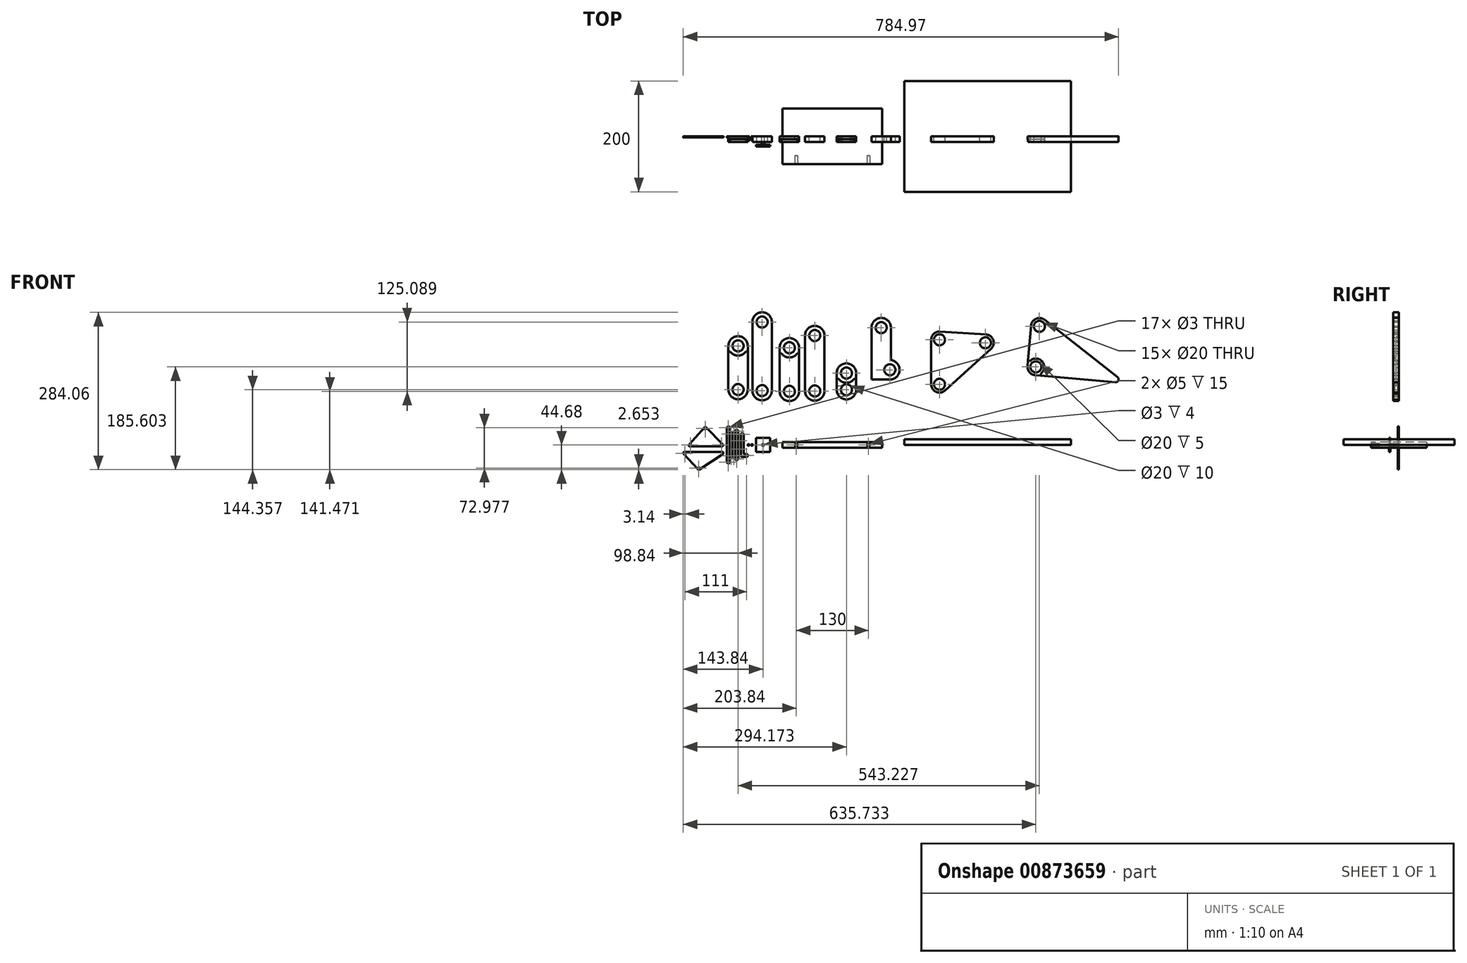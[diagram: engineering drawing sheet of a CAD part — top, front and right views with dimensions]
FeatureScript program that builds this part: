
annotation { "Feature Type Name" : "Feature", "Feature Type Description" : "" }
export const myFeature = defineFeature(function(context is Context, id is Id, definition is map)
    precondition{}
    {
        {
            var Q0;
            Q0=qCreatedBy(makeId("Front.planeOp"),FACE);
            var sketch = newSketch(context, id + "F0", { "sketchPlane" : qUnion([Q0])});
            skLineSegment(sketch, "E0", {"start": v(0, 7.5) * mm, "end": v(0, -7.5) * mm});
            skLineSegment(sketch, "E1", {"start": v(5, 7.5) * mm, "end": v(5, -7.5) * mm});
            skArc(sketch, "E2", {"start": v(5, 7.5) * mm, "mid": v(2.5, 10) * mm, "end": v(0, 7.5) * mm});
            skArc(sketch, "E3", {"start": v(0, -7.5) * mm, "mid": v(2.5, -10) * mm, "end": v(5, -7.5) * mm});
            skCircle(sketch, "E4", {"center": v(2.5, 7.5) * mm, "radius": 1.5 * mm});
            skCircle(sketch, "E5", {"center": v(2.5, -7.5) * mm, "radius": 1.5 * mm});
            skSolve(sketch);
        }
        {
            var Q0;
            Q0=makeQuery(id+"F0.imprint","IMPRINT",FACE,{"disambiguationData":[TD([[makeQuery(id+"F0.imprint","IMPRINT",EDGE,{"derivedFrom":sQuery(id+"F0.wireOp",EDGE,"E0")}),1.0]])]});
            extrude(context, id + "F1", {"entities" : qUnion([Q0]), "depth" : 2 * mm});
        }
        {
            var Q0;
            Q0=qCreatedBy(makeId("Front.planeOp"),FACE);
            var sketch = newSketch(context, id + "F2", { "sketchPlane" : qUnion([Q0])});
            skLineSegment(sketch, "E6", {"start": v(0, 25) * mm, "end": v(0, -25) * mm});
            skLineSegment(sketch, "E7", {"start": v(-5, 25) * mm, "end": v(-5, -25) * mm});
            skArc(sketch, "E8", {"start": v(0, 25) * mm, "mid": v(-2.5, 27.5) * mm, "end": v(-5, 25) * mm});
            skArc(sketch, "E9", {"start": v(-5, -25) * mm, "mid": v(-2.5, -27.5) * mm, "end": v(0, -25) * mm});
            skCircle(sketch, "E10", {"center": v(-2.5, 25) * mm, "radius": 1.5 * mm});
            skCircle(sketch, "E11", {"center": v(-2.5, -25) * mm, "radius": 1.5 * mm});
            skSolve(sketch);
        }
        {
            var Q0;
            Q0=makeQuery(id+"F2.imprint","IMPRINT",FACE,{"disambiguationData":[TD([[makeQuery(id+"F2.imprint","IMPRINT",EDGE,{"derivedFrom":sQuery(id+"F2.wireOp",EDGE,"E6")}),-1.0]])]});
            extrude(context, id + "F3", {"entities" : qUnion([Q0]), "depth" : 2 * mm});
        }
        {
            var Q0;
            Q0=qCreatedBy(makeId("Front.planeOp"),FACE);
            var sketch = newSketch(context, id + "F4", { "sketchPlane" : qUnion([Q0])});
            skLineSegment(sketch, "E12", {"start": v(-5, 19.65) * mm, "end": v(-5, -19.65) * mm});
            skLineSegment(sketch, "E13", {"start": v(-10, 19.65) * mm, "end": v(-10, -19.65) * mm});
            skArc(sketch, "E14", {"start": v(-5, 19.65) * mm, "mid": v(-7.5, 22.15) * mm, "end": v(-10, 19.65) * mm});
            skArc(sketch, "E15", {"start": v(-10, -19.65) * mm, "mid": v(-7.5, -22.15) * mm, "end": v(-5, -19.65) * mm});
            skCircle(sketch, "E16", {"center": v(-7.5, 19.65) * mm, "radius": 1.5 * mm});
            skCircle(sketch, "E17", {"center": v(-7.5, -19.65) * mm, "radius": 1.5 * mm});
            skSolve(sketch);
        }
        {
            var Q0;
            Q0=makeQuery(id+"F4.imprint","IMPRINT",FACE,{"disambiguationData":[TD([[makeQuery(id+"F4.imprint","IMPRINT",EDGE,{"derivedFrom":sQuery(id+"F4.wireOp",EDGE,"E12")}),-1.0]])]});
            extrude(context, id + "F5", {"entities" : qUnion([Q0]), "depth" : 2 * mm});
        }
        {
            var Q0;
            Q0=qCreatedBy(makeId("Front.planeOp"),FACE);
            var sketch = newSketch(context, id + "F6", { "sketchPlane" : qUnion([Q0])});
            skLineSegment(sketch, "E18", {"start": v(-10, 19.7) * mm, "end": v(-10, -19.7) * mm});
            skLineSegment(sketch, "E19", {"start": v(-15, 19.7) * mm, "end": v(-15, -19.7) * mm});
            skArc(sketch, "E20", {"start": v(-10, 19.7) * mm, "mid": v(-12.5, 22.2) * mm, "end": v(-15, 19.7) * mm});
            skArc(sketch, "E21", {"start": v(-15, -19.7) * mm, "mid": v(-12.5, -22.2) * mm, "end": v(-10, -19.7) * mm});
            skCircle(sketch, "E22", {"center": v(-12.5, 19.7) * mm, "radius": 1.5 * mm});
            skCircle(sketch, "E23", {"center": v(-12.5, -19.7) * mm, "radius": 1.5 * mm});
            skSolve(sketch);
        }
        {
            var Q0;
            Q0=makeQuery(id+"F6.imprint","IMPRINT",FACE,{"disambiguationData":[TD([[makeQuery(id+"F6.imprint","IMPRINT",EDGE,{"derivedFrom":sQuery(id+"F6.wireOp",EDGE,"E18")}),-1.0]])]});
            extrude(context, id + "F7", {"entities" : qUnion([Q0]), "depth" : 2 * mm});
        }
        {
            var Q0;
            Q0=qCreatedBy(makeId("Front.planeOp"),FACE);
            var sketch = newSketch(context, id + "F8", { "sketchPlane" : qUnion([Q0])});
            skLineSegment(sketch, "E24", {"start": v(-20, 30.95) * mm, "end": v(-20, -30.95) * mm});
            skLineSegment(sketch, "E25", {"start": v(-15, 30.95) * mm, "end": v(-15, -30.95) * mm});
            skArc(sketch, "E26", {"start": v(-15, 30.95) * mm, "mid": v(-17.5, 33.45) * mm, "end": v(-20, 30.95) * mm});
            skArc(sketch, "E27", {"start": v(-20, -30.95) * mm, "mid": v(-17.5, -33.45) * mm, "end": v(-15, -30.95) * mm});
            skCircle(sketch, "E28", {"center": v(-17.5, -30.95) * mm, "radius": 1.5 * mm});
            skCircle(sketch, "E29", {"center": v(-17.5, 30.95) * mm, "radius": 1.5 * mm});
            skSolve(sketch);
        }
        {
            var Q0;
            Q0=makeQuery(id+"F8.imprint","IMPRINT",FACE,{"disambiguationData":[TD([[makeQuery(id+"F8.imprint","IMPRINT",EDGE,{"derivedFrom":sQuery(id+"F8.wireOp",EDGE,"E24")}),1.0]])]});
            extrude(context, id + "F9", {"entities" : qUnion([Q0]), "depth" : 2 * mm});
        }
        {
            var Q0;
            Q0=qCreatedBy(makeId("Front.planeOp"),FACE);
            var sketch = newSketch(context, id + "F10", { "sketchPlane" : qUnion([Q0])});
            skLineSegment(sketch, "E30", {"start": v(-58.92, 29.76) * mm, "end": v(-30, 0) * mm, "construction": true});
            skLineSegment(sketch, "E31", {"start": v(-30, 0) * mm, "end": v(-85.8, 0) * mm, "construction": true});
            skLineSegment(sketch, "E32", {"start": v(-85.8, 0) * mm, "end": v(-58.92, 29.76) * mm, "construction": true});
            skCircle(sketch, "E33", {"center": v(-85.8, 0) * mm, "radius": 1.5 * mm});
            skCircle(sketch, "E34", {"center": v(-30, 0) * mm, "radius": 1.5 * mm});
            skCircle(sketch, "E35", {"center": v(-58.92, 29.76) * mm, "radius": 1.5 * mm});
            skLineSegment(sketch, "E36", {"start": v(-91.43, -2.5) * mm, "end": v(-24.08, -2.5) * mm});
            skLineSegment(sketch, "E37", {"start": v(-59, 33.42) * mm, "end": v(-91.43, -2.5) * mm});
            skLineSegment(sketch, "E38", {"start": v(-59, 33.42) * mm, "end": v(-24.08, -2.5) * mm});
            skSolve(sketch);
        }
        {
            var Q0;
            Q0=makeQuery(id+"F10.imprint","IMPRINT",FACE,{"disambiguationData":[TD([[makeQuery(id+"F10.imprint","IMPRINT",EDGE,{"derivedFrom":sQuery(id+"F10.wireOp",EDGE,"E33")}),-1.0]])]});
            extrude(context, id + "F11", {"entities" : qUnion([Q0]), "depth" : 2 * mm});
        }
        {
            var Q0;
            Q0=makeQuery(id+"F11.opExtrude","SWEPT_EDGE",EDGE,{"disambiguationData":[OSD([sQuery(id+"F10.wireOp",EDGE,"E36"),sQuery(id+"F10.wireOp",EDGE,"E37")])]});
            var Q1;
            Q1=makeQuery(id+"F11.opExtrude","SWEPT_EDGE",EDGE,{"disambiguationData":[OSD([sQuery(id+"F10.wireOp",EDGE,"E36"),sQuery(id+"F10.wireOp",EDGE,"E38")])]});
            var Q2;
            Q2=makeQuery(id+"F11.opExtrude","SWEPT_EDGE",EDGE,{"disambiguationData":[OSD([sQuery(id+"F10.wireOp",EDGE,"E37"),sQuery(id+"F10.wireOp",EDGE,"E38")])]});
            fillet(context, id + "F12", {"entities" : qUnion([Q0, Q1, Q2]), "radius" : 2 * mm, "tangentPropagation" : true, "allowEdgeOverflow" : false});
        }
        {
            var Q0;
            Q0=qCreatedBy(makeId("Front.planeOp"),FACE);
            var sketch = newSketch(context, id + "F13", { "sketchPlane" : qUnion([Q0])});
            skLineSegment(sketch, "E39", {"start": v(-95.7, -15) * mm, "end": v(-30, -15) * mm, "construction": true});
            skLineSegment(sketch, "E40", {"start": v(-30, -15) * mm, "end": v(-70.87, -42.03) * mm, "construction": true});
            skLineSegment(sketch, "E41", {"start": v(-70.87, -42.03) * mm, "end": v(-95.7, -15) * mm, "construction": true});
            skCircle(sketch, "E42", {"center": v(-95.7, -15) * mm, "radius": 1.5 * mm});
            skCircle(sketch, "E43", {"center": v(-70.87, -42.03) * mm, "radius": 1.5 * mm});
            skLineSegment(sketch, "E44", {"start": v(-101.4, -12.5) * mm, "end": v(-21.69, -12.5) * mm});
            skLineSegment(sketch, "E45", {"start": v(-21.69, -12.5) * mm, "end": v(-71.27, -45.29) * mm});
            skLineSegment(sketch, "E46", {"start": v(-71.27, -45.29) * mm, "end": v(-101.4, -12.5) * mm});
            skSolve(sketch);
        }
        {
            var Q0;
            Q0=makeQuery(id+"F13.imprint","IMPRINT",FACE,{"disambiguationData":[TD([[makeQuery(id+"F13.imprint","IMPRINT",EDGE,{"derivedFrom":sQuery(id+"F13.wireOp",EDGE,"E42")}),-1.0]])]});
            extrude(context, id + "F14", {"entities" : qUnion([Q0]), "depth" : 2 * mm});
        }
        {
            var Q0;
            Q0=makeQuery(id+"F14.opExtrude","SWEPT_EDGE",EDGE,{"disambiguationData":[OSD([sQuery(id+"F13.wireOp",EDGE,"E44"),sQuery(id+"F13.wireOp",EDGE,"E46")])]});
            var Q1;
            Q1=makeQuery(id+"F14.opExtrude","SWEPT_EDGE",EDGE,{"disambiguationData":[OSD([sQuery(id+"F13.wireOp",EDGE,"E45"),sQuery(id+"F13.wireOp",EDGE,"E46")])]});
            var Q2;
            Q2=makeQuery(id+"F14.opExtrude","SWEPT_EDGE",EDGE,{"disambiguationData":[OSD([sQuery(id+"F13.wireOp",EDGE,"E44"),sQuery(id+"F13.wireOp",EDGE,"E45")])]});
            fillet(context, id + "F15", {"entities" : qUnion([Q0, Q1, Q2]), "radius" : 2 * mm, "tangentPropagation" : true, "allowEdgeOverflow" : false});
        }
        {
            var Q0;
            Q0=qCreatedBy(makeId("Front.planeOp"),FACE);
            var sketch = newSketch(context, id + "F16", { "sketchPlane" : qUnion([Q0])});
            skLineSegment(sketch, "E47", {"start": v(7.5, 19) * mm, "end": v(7.5, -19) * mm, "construction": true});
            skLineSegment(sketch, "E48", {"start": v(7.5, -19) * mm, "end": v(15.3, -19) * mm, "construction": true});
            skArc(sketch, "E49", {"start": v(10, 19) * mm, "mid": v(7.5, 21.5) * mm, "end": v(5, 19) * mm});
            skArc(sketch, "E50", {"start": v(15.3, -21.5) * mm, "mid": v(17.8, -19) * mm, "end": v(15.3, -16.5) * mm});
            skLineSegment(sketch, "E51", {"start": v(5, 19) * mm, "end": v(5, -21.5) * mm});
            skLineSegment(sketch, "E52", {"start": v(15.3, -21.5) * mm, "end": v(5, -21.5) * mm});
            skLineSegment(sketch, "E53", {"start": v(10, 19) * mm, "end": v(10, -16.5) * mm});
            skLineSegment(sketch, "E54", {"start": v(15.3, -16.5) * mm, "end": v(10, -16.5) * mm});
            skCircle(sketch, "E55", {"center": v(7.5, 19) * mm, "radius": 1.5 * mm});
            skCircle(sketch, "E56", {"center": v(15.3, -19) * mm, "radius": 1.5 * mm});
            skSolve(sketch);
        }
        {
            var Q0;
            Q0=makeQuery(id+"F16.imprint","IMPRINT",FACE,{"disambiguationData":[TD([[makeQuery(id+"F16.imprint","IMPRINT",EDGE,{"derivedFrom":sQuery(id+"F16.wireOp",EDGE,"E49")}),1.0]])]});
            extrude(context, id + "F17", {"entities" : qUnion([Q0]), "depth" : 2 * mm});
        }
        {
            var Q0;
            Q0=qCreatedBy(makeId("Front.planeOp"),FACE);
            var sketch = newSketch(context, id + "F18", { "sketchPlane" : qUnion([Q0])});
            skCircle(sketch, "E57", {"center": v(24.95, 0) * mm, "radius": 1.5 * mm});
            skSolve(sketch);
        }
        {
            var Q0;
            Q0=makeQuery(id+"F18.imprint","IMPRINT",FACE,{"disambiguationData":[TD([[makeQuery(id+"F18.imprint","IMPRINT",EDGE,{"derivedFrom":sQuery(id+"F18.wireOp",EDGE,"E57")}),1.0]])]});
            extrude(context, id + "F19", {"entities" : qUnion([Q0]), "depth" : 6 * mm});
        }
        {
            var Q0;
            Q0=qCreatedBy(makeId("Front.planeOp"),FACE);
            var sketch = newSketch(context, id + "F20", { "sketchPlane" : qUnion([Q0])});
            skCircle(sketch, "E58", {"center": v(45, 0) * mm, "radius": 2.5 * mm});
            skSolve(sketch);
        }
        {
            var Q0;
            Q0=makeQuery(id+"F20.imprint","IMPRINT",FACE,{"disambiguationData":[TD([[makeQuery(id+"F20.imprint","IMPRINT",EDGE,{"derivedFrom":sQuery(id+"F20.wireOp",EDGE,"E58")}),1.0]])]});
            extrude(context, id + "F21", {"entities" : qUnion([Q0]), "depth" : 15 * mm, "offsetDistance" : 25 * mm});
        }
        {
            var Q0;
            Q0=makeQuery(id+"F21.opExtrude","CAP_FACE",FACE,{"disambiguationData":[OSD([sQuery(id+"F20.wireOp",EDGE,"E58")])],"isStart":false});
            var sketch = newSketch(context, id + "F22", { "sketchPlane" : qUnion([Q0])});
            skLineSegment(sketch, "E59.bottom", {"start": v(32.5, 12.5) * mm, "end": v(57.5, 12.5) * mm});
            skLineSegment(sketch, "E59.top", {"start": v(32.5, -12.5) * mm, "end": v(57.5, -12.5) * mm});
            skLineSegment(sketch, "E59.left", {"start": v(32.5, 12.5) * mm, "end": v(32.5, -12.5) * mm});
            skLineSegment(sketch, "E59.right", {"start": v(57.5, 12.5) * mm, "end": v(57.5, -12.5) * mm});
            skCircle(sketch, "E60.0", {"center": v(45, 0) * mm, "radius": 2.5 * mm, "construction": true});
            skSolve(sketch);
        }
        {
            var Q0;
            Q0=makeQuery(id+"F22.imprint","IMPRINT",FACE,{"disambiguationData":[TD([[makeQuery(id+"F22.imprint","IMPRINT",EDGE,{"derivedFrom":sQuery(id+"F22.wireOp",EDGE,"E59.bottom")}),-1.0]])]});
            var Q1;
            Q1=makeQuery(id+"F22.imprint","IMPRINT",FACE,{"disambiguationData":[TD([[makeQuery(id+"F22.imprint","IMPRINT",EDGE,{"derivedFrom":makeQuery(id+"F21.opExtrude","CAP_EDGE",EDGE,{"disambiguationData":[OSD([sQuery(id+"F20.wireOp",EDGE,"E58")])],"isStart":false})}),1.0]])]});
            extrude(context, id + "F23", {"entities" : qUnion([Q0, Q1]), "operationType" : NewBodyOperationType.ADD, "depth" : 3 * mm});
        }
        {
            var Q0;
            Q0=makeQuery(id+"F23.opExtrude","CAP_FACE",FACE,{"disambiguationData":[OSD([sQuery(id+"F22.wireOp",EDGE,"E59.bottom"),sQuery(id+"F22.wireOp",EDGE,"E59.top"),sQuery(id+"F22.wireOp",EDGE,"E59.left"),sQuery(id+"F22.wireOp",EDGE,"E59.right")])],"isStart":false});
            var sketch = newSketch(context, id + "F24", { "sketchPlane" : qUnion([Q0])});
            skCircle(sketch, "E61", {"center": v(45, 0) * mm, "radius": 1.5 * mm});
            skSolve(sketch);
        }
        {
            var Q0;
            Q0=makeQuery(id+"F24.imprint","IMPRINT",FACE,{"disambiguationData":[TD([[makeQuery(id+"F24.imprint","IMPRINT",EDGE,{"derivedFrom":sQuery(id+"F24.wireOp",EDGE,"E61")}),1.0]])]});
            extrude(context, id + "F25", {"entities" : qUnion([Q0]), "operationType" : NewBodyOperationType.REMOVE, "oppositeDirection" : true, "depth" : 4 * mm});
        }
        {
            var Q0;
            Q0=qCreatedBy(makeId("Front.planeOp"),FACE);
            var sketch = newSketch(context, id + "F26", { "sketchPlane" : qUnion([Q0])});
            skCircle(sketch, "E62", {"center": v(18.95, 0) * mm, "radius": 1.5 * mm});
            skSolve(sketch);
        }
        {
            var Q0;
            Q0=makeQuery(id+"F26.imprint","IMPRINT",FACE,{"disambiguationData":[TD([[makeQuery(id+"F26.imprint","IMPRINT",EDGE,{"derivedFrom":sQuery(id+"F26.wireOp",EDGE,"E62")}),1.0]])]});
            extrude(context, id + "F27", {"entities" : qUnion([Q0]), "depth" : 8 * mm});
        }
        {
            var Q0;
            Q0=qCreatedBy(makeId("Top.planeOp"),FACE);
            var sketch = newSketch(context, id + "F28", { "sketchPlane" : qUnion([Q0])});
            skLineSegment(sketch, "E63.bottom", {"start": v(80, 50) * mm, "end": v(260, 50) * mm});
            skLineSegment(sketch, "E63.top", {"start": v(80, -50) * mm, "end": v(260, -50) * mm});
            skLineSegment(sketch, "E63.left", {"start": v(80, 50) * mm, "end": v(80, -50) * mm});
            skLineSegment(sketch, "E63.right", {"start": v(260, 50) * mm, "end": v(260, -50) * mm});
            skSolve(sketch);
        }
        {
            var Q0;
            Q0=qSketchRegion(id+"F28",true);
            extrude(context, id + "F29", {"entities" : qUnion([Q0]), "depth" : 5 * mm, "offsetDistance" : 25 * mm, "hasSecondDirection" : true, "secondDirectionOppositeDirection" : true, "secondDirectionDepth" : 5 * mm});
        }
        {
            var Q0;
            Q0=makeQuery(id+"F29.opExtrude","SWEPT_FACE",FACE,{"disambiguationData":[OSD([sQuery(id+"F28.wireOp",EDGE,"E63.top")])]});
            var sketch = newSketch(context, id + "F30", { "sketchPlane" : qUnion([Q0])});
            skCircle(sketch, "E64", {"center": v(105, 0) * mm, "radius": 2.5 * mm});
            skPoint(sketch, "E64.centerSnap0", {"position": v(80, 0) * mm});
            skCircle(sketch, "E65", {"center": v(235, 0) * mm, "radius": 2.5 * mm});
            skSolve(sketch);
        }
        {
            var Q0;
            Q0=qSketchRegion(id+"F30",true);
            extrude(context, id + "F31", {"entities" : qUnion([Q0]), "operationType" : NewBodyOperationType.REMOVE, "oppositeDirection" : true, "depth" : 15 * mm, "offsetDistance" : 25 * mm});
        }
        {
            var Q0;
            Q0=qCreatedBy(makeId("Top.planeOp"),FACE);
            var sketch = newSketch(context, id + "F32", { "sketchPlane" : qUnion([Q0])});
            skLineSegment(sketch, "E66.bottom", {"start": v(300, 100) * mm, "end": v(600, 100) * mm});
            skLineSegment(sketch, "E66.top", {"start": v(300, -100) * mm, "end": v(600, -100) * mm});
            skLineSegment(sketch, "E66.left", {"start": v(300, 100) * mm, "end": v(300, -100) * mm});
            skLineSegment(sketch, "E66.right", {"start": v(600, 100) * mm, "end": v(600, -100) * mm});
            skSolve(sketch);
        }
        {
            var Q0;
            Q0=qSketchRegion(id+"F32",true);
            extrude(context, id + "F33", {"entities" : qUnion([Q0]), "depth" : 10 * mm, "offsetDistance" : 25 * mm});
        }
        {
            var Q0;
            Q0=qCreatedBy(makeId("Front.planeOp"),FACE);
            var sketch = newSketch(context, id + "F34", { "sketchPlane" : qUnion([Q0])});
            skCircle(sketch, "E67", {"center": v(0, 178.8) * mm, "radius": 10 * mm});
            skCircle(sketch, "E68", {"center": v(0, 100) * mm, "radius": 10 * mm});
            skArc(sketch, "E69", {"start": v(17.5, 178.8) * mm, "mid": v(0, 196.3) * mm, "end": v(-17.5, 178.8) * mm});
            skArc(sketch, "E70", {"start": v(-17.5, 100) * mm, "mid": v(0, 82.5) * mm, "end": v(17.5, 100) * mm});
            skLineSegment(sketch, "E71", {"start": v(-17.5, 178.8) * mm, "end": v(-17.5, 100) * mm});
            skLineSegment(sketch, "E72", {"start": v(17.5, 178.8) * mm, "end": v(17.5, 100) * mm});
            skSolve(sketch);
        }
        {
            var Q0;
            Q0=qSketchRegion(id+"F34",true);
            extrude(context, id + "F35", {"entities" : qUnion([Q0]), "depth" : 10 * mm, "offsetDistance" : 25 * mm});
        }
        {
            var Q0;
            Q0=qCreatedBy(makeId("Front.planeOp"),FACE);
            var sketch = newSketch(context, id + "F36", { "sketchPlane" : qUnion([Q0])});
            skCircle(sketch, "E73", {"center": v(43.37, 98.08) * mm, "radius": 10 * mm});
            skArc(sketch, "E74", {"start": v(25.87, 98.08) * mm, "mid": v(43.37, 80.58) * mm, "end": v(60.87, 98.08) * mm});
            skArc(sketch, "E75", {"start": v(60.87, 221.88) * mm, "mid": v(43.37, 239.38) * mm, "end": v(25.87, 221.88) * mm});
            skCircle(sketch, "E76", {"center": v(43.37, 221.88) * mm, "radius": 10 * mm});
            skLineSegment(sketch, "E77", {"start": v(25.87, 221.88) * mm, "end": v(25.87, 98.08) * mm});
            skLineSegment(sketch, "E78", {"start": v(60.87, 221.88) * mm, "end": v(60.87, 98.08) * mm});
            skSolve(sketch);
        }
        {
            var Q0;
            Q0=qSketchRegion(id+"F36",true);
            extrude(context, id + "F37", {"entities" : qUnion([Q0]), "depth" : 10 * mm, "offsetDistance" : 25 * mm});
        }
        {
            var Q0;
            Q0=qCreatedBy(makeId("Front.planeOp"),FACE);
            var sketch = newSketch(context, id + "F38", { "sketchPlane" : qUnion([Q0])});
            skCircle(sketch, "E79", {"center": v(92.5, 96.8) * mm, "radius": 10 * mm});
            skCircle(sketch, "E80", {"center": v(92.5, 175.4) * mm, "radius": 10 * mm});
            skArc(sketch, "E81", {"start": v(110, 175.4) * mm, "mid": v(92.5, 192.9) * mm, "end": v(75, 175.4) * mm});
            skArc(sketch, "E82", {"start": v(75, 96.8) * mm, "mid": v(92.5, 79.3) * mm, "end": v(110, 96.8) * mm});
            skLineSegment(sketch, "E83", {"start": v(75, 175.4) * mm, "end": v(75, 96.8) * mm});
            skLineSegment(sketch, "E84", {"start": v(110, 175.4) * mm, "end": v(110, 96.8) * mm});
            skSolve(sketch);
        }
        {
            var Q0;
            Q0=qSketchRegion(id+"F38",true);
            extrude(context, id + "F39", {"entities" : qUnion([Q0]), "depth" : 10 * mm, "offsetDistance" : 25 * mm});
        }
        {
            var Q0;
            Q0=qCreatedBy(makeId("Front.planeOp"),FACE);
            var sketch = newSketch(context, id + "F40", { "sketchPlane" : qUnion([Q0])});
            skCircle(sketch, "E85", {"center": v(138.24, 97.46) * mm, "radius": 10 * mm});
            skCircle(sketch, "E86", {"center": v(138.24, 197.46) * mm, "radius": 10 * mm});
            skArc(sketch, "E87", {"start": v(155.74, 197.46) * mm, "mid": v(138.24, 214.96) * mm, "end": v(120.74, 197.46) * mm});
            skArc(sketch, "E88", {"start": v(120.74, 97.46) * mm, "mid": v(138.24, 79.96) * mm, "end": v(155.74, 97.46) * mm});
            skLineSegment(sketch, "E89", {"start": v(120.74, 197.46) * mm, "end": v(120.74, 97.46) * mm});
            skLineSegment(sketch, "E90", {"start": v(155.74, 197.46) * mm, "end": v(155.74, 97.46) * mm});
            skSolve(sketch);
        }
        {
            var Q0;
            Q0=qSketchRegion(id+"F40",true);
            extrude(context, id + "F41", {"entities" : qUnion([Q0]), "depth" : 10 * mm, "offsetDistance" : 25 * mm});
        }
        {
            var Q0;
            Q0=qCreatedBy(makeId("Front.planeOp"),FACE);
            var sketch = newSketch(context, id + "F42", { "sketchPlane" : qUnion([Q0])});
            skCircle(sketch, "E91", {"center": v(195.33, 99.68) * mm, "radius": 10 * mm});
            skCircle(sketch, "E92", {"center": v(195.33, 129.68) * mm, "radius": 10 * mm});
            skArc(sketch, "E93", {"start": v(212.83, 129.68) * mm, "mid": v(195.33, 147.18) * mm, "end": v(177.83, 129.68) * mm});
            skArc(sketch, "E94", {"start": v(177.83, 99.68) * mm, "mid": v(195.33, 82.18) * mm, "end": v(212.83, 99.68) * mm});
            skLineSegment(sketch, "E95", {"start": v(177.83, 129.68) * mm, "end": v(177.83, 99.68) * mm});
            skLineSegment(sketch, "E96", {"start": v(212.83, 129.68) * mm, "end": v(212.83, 99.68) * mm});
            skSolve(sketch);
        }
        {
            var Q0;
            Q0=qSketchRegion(id+"F42",true);
            extrude(context, id + "F43", {"entities" : qUnion([Q0]), "depth" : 10 * mm, "offsetDistance" : 25 * mm});
        }
        {
            var Q0;
            Q0=qCreatedBy(makeId("Front.planeOp"),FACE);
            var sketch = newSketch(context, id + "F44", { "sketchPlane" : qUnion([Q0])});
            skLineSegment(sketch, "E97", {"start": v(258.08, 211.66) * mm, "end": v(258.08, 135.66) * mm, "construction": true});
            skLineSegment(sketch, "E98", {"start": v(258.08, 135.66) * mm, "end": v(273.68, 135.66) * mm, "construction": true});
            skCircle(sketch, "E99", {"center": v(258.08, 211.66) * mm, "radius": 10 * mm});
            skCircle(sketch, "E100", {"center": v(273.68, 135.66) * mm, "radius": 10 * mm});
            skArc(sketch, "E101", {"start": v(275.58, 211.66) * mm, "mid": v(258.08, 229.16) * mm, "end": v(240.58, 211.66) * mm});
            skArc(sketch, "E102", {"start": v(273.68, 118.16) * mm, "mid": v(291.15, 134.7) * mm, "end": v(275.58, 153.05) * mm});
            skLineSegment(sketch, "E103", {"start": v(275.58, 211.66) * mm, "end": v(275.58, 153.05) * mm});
            skLineSegment(sketch, "E104", {"start": v(240.58, 211.66) * mm, "end": v(240.58, 118.16) * mm});
            skLineSegment(sketch, "E105", {"start": v(240.58, 118.16) * mm, "end": v(273.68, 118.16) * mm});
            skSolve(sketch);
        }
        {
            var Q0;
            Q0=qSketchRegion(id+"F44",true);
            extrude(context, id + "F45", {"entities" : qUnion([Q0]), "depth" : 10 * mm, "offsetDistance" : 25 * mm});
        }
        {
            var Q0;
            Q0=qCreatedBy(makeId("Front.planeOp"),FACE);
            var sketch = newSketch(context, id + "F46", { "sketchPlane" : qUnion([Q0])});
            skLineSegment(sketch, "E106", {"start": v(363.12, 189.73) * mm, "end": v(363.12, 109.53) * mm, "construction": true});
            skLineSegment(sketch, "E107", {"start": v(363.12, 109.53) * mm, "end": v(445.94, 184.33) * mm, "construction": true});
            skLineSegment(sketch, "E108", {"start": v(445.94, 184.33) * mm, "end": v(363.12, 189.73) * mm, "construction": true});
            skCircle(sketch, "E109", {"center": v(363.12, 189.73) * mm, "radius": 10 * mm});
            skCircle(sketch, "E110", {"center": v(445.94, 184.33) * mm, "radius": 10 * mm});
            skCircle(sketch, "E111", {"center": v(363.12, 109.53) * mm, "radius": 10 * mm});
            skArc(sketch, "E112", {"start": v(364.1, 204.7) * mm, "mid": v(352.86, 200.68) * mm, "end": v(348.12, 189.73) * mm});
            skLineSegment(sketch, "E113", {"start": v(348.12, 189.73) * mm, "end": v(348.12, 109.53) * mm});
            skLineSegment(sketch, "E114.0", {"start": v(446.92, 199.3) * mm, "end": v(364.1, 204.7) * mm});
            skLineSegment(sketch, "E114.1", {"start": v(373.17, 98.4) * mm, "end": v(456, 173.2) * mm});
            skPoint(sketch, "E115.visualSharp", {"position": v(482.34, 196.98) * mm});
            skArc(sketch, "E115.filletArc", {"start": v(456, 173.2) * mm, "mid": v(460.1, 189.25) * mm, "end": v(446.92, 199.3) * mm});
            skArc(sketch, "E116", {"start": v(348.12, 109.53) * mm, "mid": v(357.02, 95.82) * mm, "end": v(373.17, 98.4) * mm});
            skSolve(sketch);
        }
        {
            var Q0;
            Q0=qSketchRegion(id+"F46",true);
            extrude(context, id + "F47", {"entities" : qUnion([Q0]), "depth" : 10 * mm, "offsetDistance" : 25 * mm});
        }
        {
            var Q0;
            Q0=qCreatedBy(makeId("Front.planeOp"),FACE);
            var sketch = newSketch(context, id + "F48", { "sketchPlane" : qUnion([Q0])});
            skLineSegment(sketch, "E117", {"start": v(536.9, 140.92) * mm, "end": v(543.23, 214.05) * mm, "construction": true});
            skLineSegment(sketch, "E118", {"start": v(543.23, 214.05) * mm, "end": v(648.58, 131.25) * mm, "construction": true});
            skLineSegment(sketch, "E119", {"start": v(648.58, 131.25) * mm, "end": v(536.9, 140.92) * mm, "construction": true});
            skCircle(sketch, "E120", {"center": v(543.23, 214.05) * mm, "radius": 10 * mm});
            skCircle(sketch, "E121", {"center": v(536.9, 140.92) * mm, "radius": 10 * mm});
            skArc(sketch, "E122", {"start": v(552.5, 225.84) * mm, "mid": v(537.26, 227.81) * mm, "end": v(528.28, 215.34) * mm});
            skArc(sketch, "E123", {"start": v(521.95, 142.22) * mm, "mid": v(525.41, 131.27) * mm, "end": v(535.6, 125.98) * mm});
            skLineSegment(sketch, "E124", {"start": v(536.9, 140.92) * mm, "end": v(467.82, 146.9) * mm, "construction": true});
            skLineSegment(sketch, "E125", {"start": v(521.95, 142.22) * mm, "end": v(528.28, 215.34) * mm});
            skLineSegment(sketch, "E126", {"start": v(535.6, 125.98) * mm, "end": v(680.7, 113.41) * mm});
            skLineSegment(sketch, "E127", {"start": v(552.5, 225.84) * mm, "end": v(684.22, 122.32) * mm});
            skPoint(sketch, "E128.visualSharp", {"position": v(697.4, 111.97) * mm});
            skArc(sketch, "E128.filletArc", {"start": v(680.7, 113.41) * mm, "mid": v(685.78, 116.56) * mm, "end": v(684.22, 122.32) * mm});
            skSolve(sketch);
        }
        {
            var Q0;
            Q0=qSketchRegion(id+"F48",true);
            extrude(context, id + "F49", {"entities" : qUnion([Q0]), "depth" : 10 * mm, "offsetDistance" : 25 * mm});
        }
        {
            var Q0;
            Q0=makeQuery(id+"F35.opExtrude","CAP_FACE",FACE,{"disambiguationData":[OSD([sQuery(id+"F34.wireOp",EDGE,"E67"),sQuery(id+"F34.wireOp",EDGE,"E68"),sQuery(id+"F34.wireOp",EDGE,"E69"),sQuery(id+"F34.wireOp",EDGE,"E70"),sQuery(id+"F34.wireOp",EDGE,"E71"),sQuery(id+"F34.wireOp",EDGE,"E72")])],"isStart":false});
            var sketch = newSketch(context, id + "F50", { "sketchPlane" : qUnion([Q0])});
            skArc(sketch, "E129", {"start": v(-14.36, 168.8) * mm, "mid": v(0, 161.3) * mm, "end": v(14.36, 168.8) * mm});
            skLineSegment(sketch, "E130", {"start": v(-14.36, 168.8) * mm, "end": v(-17.5, 168.8) * mm});
            skLineSegment(sketch, "E131", {"start": v(14.36, 168.8) * mm, "end": v(17.5, 168.8) * mm});
            skLineSegment(sketch, "E132", {"start": v(-17.5, 168.8) * mm, "end": v(-17.5, 178.8) * mm});
            skLineSegment(sketch, "E133", {"start": v(17.5, 168.8) * mm, "end": v(17.5, 178.8) * mm});
            skArc(sketch, "E134.trimOffspring", {"start": v(17.5, 178.8) * mm, "mid": v(0, 196.3) * mm, "end": v(-17.5, 178.8) * mm});
            skSolve(sketch);
        }
        {
            var Q0;
            Q0=qSketchRegion(id+"F50",true);
            extrude(context, id + "F51", {"entities" : qUnion([Q0]), "operationType" : NewBodyOperationType.REMOVE, "oppositeDirection" : true, "depth" : 5 * mm, "offsetDistance" : 25 * mm});
        }
        {
            var Q0;
            Q0=makeQuery(id+"F43.opExtrude","CAP_FACE",FACE,{"disambiguationData":[OSD([sQuery(id+"F42.wireOp",EDGE,"E91"),sQuery(id+"F42.wireOp",EDGE,"E92"),sQuery(id+"F42.wireOp",EDGE,"E93"),sQuery(id+"F42.wireOp",EDGE,"E94"),sQuery(id+"F42.wireOp",EDGE,"E95"),sQuery(id+"F42.wireOp",EDGE,"E96")])],"isStart":false});
            var sketch = newSketch(context, id + "F52", { "sketchPlane" : qUnion([Q0])});
            skArc(sketch, "E135", {"start": v(180.97, 119.68) * mm, "mid": v(195.33, 112.18) * mm, "end": v(209.7, 119.68) * mm});
            skLineSegment(sketch, "E136", {"start": v(177.83, 119.68) * mm, "end": v(180.97, 119.68) * mm});
            skLineSegment(sketch, "E137", {"start": v(209.7, 119.68) * mm, "end": v(212.83, 119.68) * mm});
            skLineSegment(sketch, "E138", {"start": v(177.83, 129.68) * mm, "end": v(177.83, 119.68) * mm});
            skLineSegment(sketch, "E139", {"start": v(212.83, 119.68) * mm, "end": v(212.83, 129.68) * mm});
            skArc(sketch, "E140.trimOffspring", {"start": v(212.83, 129.68) * mm, "mid": v(195.33, 147.18) * mm, "end": v(177.83, 129.68) * mm});
            skSolve(sketch);
        }
        {
            var Q0;
            Q0=qSketchRegion(id+"F52",true);
            extrude(context, id + "F53", {"entities" : qUnion([Q0]), "operationType" : NewBodyOperationType.REMOVE, "oppositeDirection" : true, "depth" : 5 * mm, "offsetDistance" : 25 * mm});
        }
        {
            var Q0;
            Q0=makeQuery(id+"F39.opExtrude","CAP_FACE",FACE,{"disambiguationData":[OSD([sQuery(id+"F38.wireOp",EDGE,"E79"),sQuery(id+"F38.wireOp",EDGE,"E80"),sQuery(id+"F38.wireOp",EDGE,"E81"),sQuery(id+"F38.wireOp",EDGE,"E82"),sQuery(id+"F38.wireOp",EDGE,"E83"),sQuery(id+"F38.wireOp",EDGE,"E84")])],"isStart":false});
            var sketch = newSketch(context, id + "F54", { "sketchPlane" : qUnion([Q0])});
            skArc(sketch, "E141", {"start": v(78.14, 165.4) * mm, "mid": v(92.5, 157.9) * mm, "end": v(106.87, 165.4) * mm});
            skLineSegment(sketch, "E142", {"start": v(75, 165.4) * mm, "end": v(78.14, 165.4) * mm});
            skLineSegment(sketch, "E143.trimOffspring", {"start": v(106.87, 165.4) * mm, "end": v(110, 165.4) * mm});
            skLineSegment(sketch, "E144", {"start": v(75, 165.4) * mm, "end": v(75, 175.4) * mm});
            skLineSegment(sketch, "E145", {"start": v(110, 165.4) * mm, "end": v(110, 175.4) * mm});
            skArc(sketch, "E146.trimOffspring", {"start": v(110, 175.4) * mm, "mid": v(92.5, 192.9) * mm, "end": v(75, 175.4) * mm});
            skSolve(sketch);
        }
        {
            var Q0;
            Q0=qSketchRegion(id+"F54",true);
            extrude(context, id + "F55", {"entities" : qUnion([Q0]), "operationType" : NewBodyOperationType.REMOVE, "oppositeDirection" : true, "depth" : 5 * mm, "offsetDistance" : 25 * mm});
        }
        {
            var Q0;
            Q0=makeQuery(id+"F49.opExtrude","CAP_FACE",FACE,{"disambiguationData":[OSD([sQuery(id+"F48.wireOp",EDGE,"E120"),sQuery(id+"F48.wireOp",EDGE,"E121"),sQuery(id+"F48.wireOp",EDGE,"E122"),sQuery(id+"F48.wireOp",EDGE,"E123"),sQuery(id+"F48.wireOp",EDGE,"E125"),sQuery(id+"F48.wireOp",EDGE,"E126"),sQuery(id+"F48.wireOp",EDGE,"E127"),sQuery(id+"F48.wireOp",EDGE,"E128.filletArc")])],"isStart":false});
            var sketch = newSketch(context, id + "F56", { "sketchPlane" : qUnion([Q0])});
            skArc(sketch, "E147", {"start": v(521.95, 142.22) * mm, "mid": v(525.41, 131.27) * mm, "end": v(535.6, 125.98) * mm});
            skLineSegment(sketch, "E148", {"start": v(526.62, 151.85) * mm, "end": v(522.81, 152.18) * mm});
            skLineSegment(sketch, "E149", {"start": v(522.81, 152.18) * mm, "end": v(521.95, 142.22) * mm});
            skLineSegment(sketch, "E150", {"start": v(545.9, 128.92) * mm, "end": v(545.56, 125.12) * mm});
            skLineSegment(sketch, "E151", {"start": v(535.6, 125.98) * mm, "end": v(545.56, 125.12) * mm});
            skArc(sketch, "E152.trimOffspring", {"start": v(545.9, 128.92) * mm, "mid": v(548.38, 150.58) * mm, "end": v(526.62, 151.85) * mm});
            skSolve(sketch);
        }
        {
            var Q0;
            Q0=qSketchRegion(id+"F56",true);
            extrude(context, id + "F57", {"entities" : qUnion([Q0]), "operationType" : NewBodyOperationType.REMOVE, "oppositeDirection" : true, "depth" : 5 * mm, "offsetDistance" : 25 * mm});
        }
        {
            var Q0;
            Q0=makeQuery(id+"F43.opExtrude","CAP_FACE",FACE,{"disambiguationData":[OSD([sQuery(id+"F42.wireOp",EDGE,"E91"),sQuery(id+"F42.wireOp",EDGE,"E92"),sQuery(id+"F42.wireOp",EDGE,"E93"),sQuery(id+"F42.wireOp",EDGE,"E94"),sQuery(id+"F42.wireOp",EDGE,"E95"),sQuery(id+"F42.wireOp",EDGE,"E96")])],"isStart":false});
            cPlane(context, id + "F58", {"entities" : qUnion([Q0]), "cplaneType" : CPlaneType.OFFSET, "offset" : 5 * mm, "oppositeDirection" : true, "width" : 150 * mm, "height" : 150 * mm});
        }
        {
            var Q0;
            Q0=qCreatedBy(id+"F58.planeOp",FACE);
            var sketch = newSketch(context, id + "F59", { "sketchPlane" : qUnion([Q0])});
            skLineSegment(sketch, "E153.bottom", {"start": v(170.34, 106.68) * mm, "end": v(225.77, 106.68) * mm});
            skLineSegment(sketch, "E153.top", {"start": v(170.34, 92.68) * mm, "end": v(225.77, 92.68) * mm});
            skLineSegment(sketch, "E153.left", {"start": v(170.34, 106.68) * mm, "end": v(170.34, 92.68) * mm});
            skLineSegment(sketch, "E153.right", {"start": v(225.77, 106.68) * mm, "end": v(225.77, 92.68) * mm});
            skCircle(sketch, "E154.0", {"center": v(195.33, 99.68) * mm, "radius": 10 * mm, "construction": true});
            skSolve(sketch);
        }
        {
            var Q0;
            Q0=qSketchRegion(id+"F59",true);
            extrude(context, id + "F60", {"entities" : qUnion([Q0]), "operationType" : NewBodyOperationType.REMOVE, "oppositeDirection" : true, "depth" : 2.5 * mm, "offsetDistance" : 25 * mm, "hasSecondDirection" : true, "secondDirectionOppositeDirection" : false, "secondDirectionDepth" : 2.5 * mm});
        }
    });
